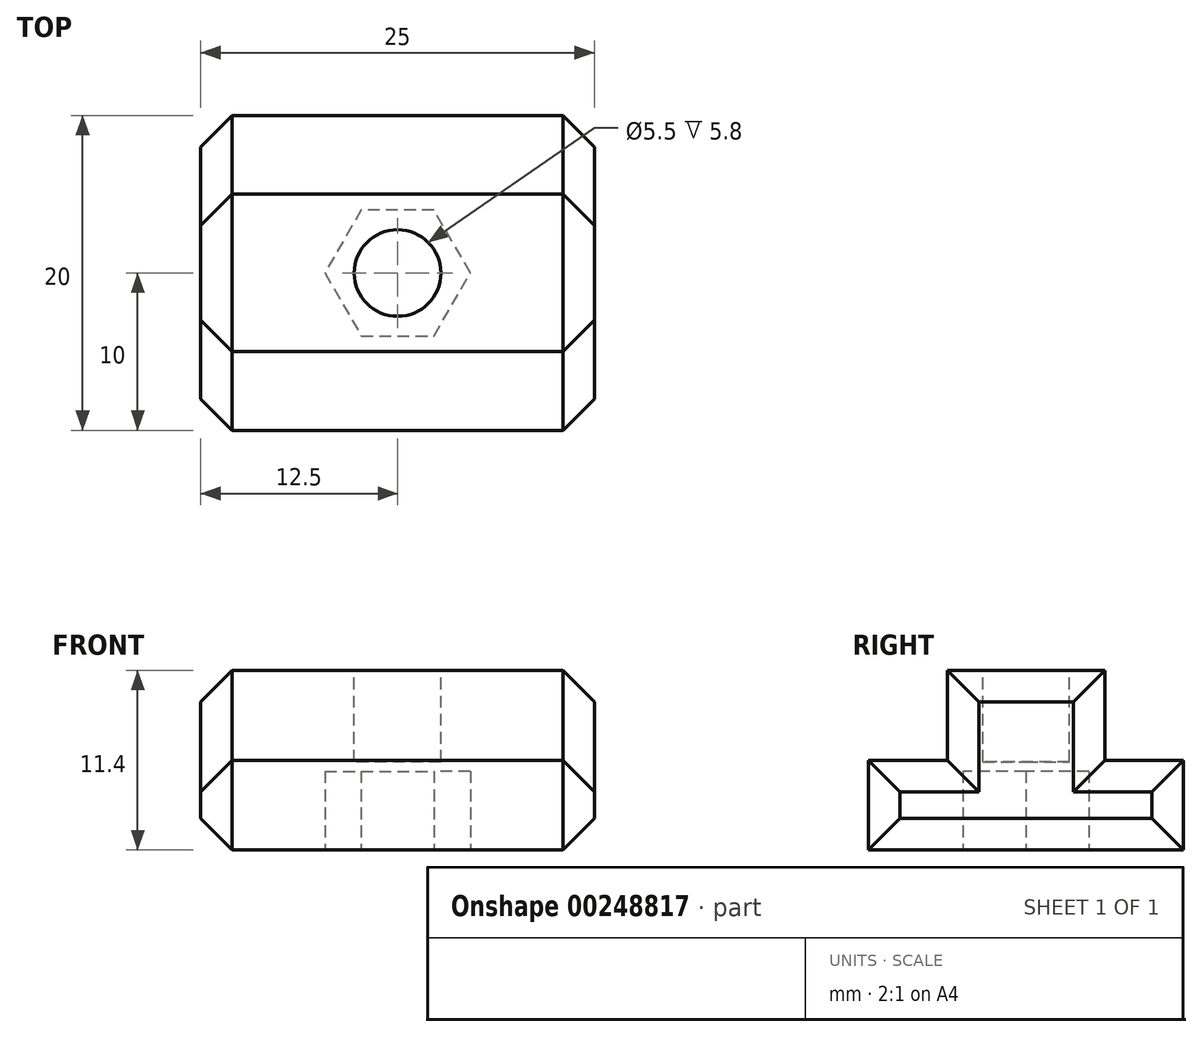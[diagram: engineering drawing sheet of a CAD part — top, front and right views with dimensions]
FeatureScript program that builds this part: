
annotation { "Feature Type Name" : "Feature", "Feature Type Description" : "" }
export const myFeature = defineFeature(function(context is Context, id is Id, definition is map)
    precondition{}
    {
        {
            var Q0;
            Q0=qCreatedBy(makeId("Right.planeOp"),FACE);
            var sketch = newSketch(context, id + "F0", { "sketchPlane" : qUnion([Q0])});
            skLineSegment(sketch, "E0", {"start": v(0, 5.7) * mm, "end": v(5, 5.7) * mm});
            skLineSegment(sketch, "E1", {"start": v(5, 5.7) * mm, "end": v(5, 0) * mm});
            skLineSegment(sketch, "E2", {"start": v(5, 0) * mm, "end": v(10, 0) * mm});
            skLineSegment(sketch, "E3", {"start": v(10, 0) * mm, "end": v(10, -5.7) * mm});
            skLineSegment(sketch, "E4", {"start": v(10, -5.7) * mm, "end": v(0, -5.7) * mm});
            skLineSegment(sketch, "E5.MirrorCS", {"start": v(0, 5.7) * mm, "end": v(-5, 5.7) * mm});
            skLineSegment(sketch, "E6.MirrorCS", {"start": v(-5, 0) * mm, "end": v(-10, 0) * mm});
            skLineSegment(sketch, "E7.MirrorCS", {"start": v(-10, -5.7) * mm, "end": v(0, -5.7) * mm});
            skLineSegment(sketch, "E8.MirrorCS", {"start": v(-5, 5.7) * mm, "end": v(-5, 0) * mm});
            skLineSegment(sketch, "E9.MirrorCS", {"start": v(-10, 0) * mm, "end": v(-10, -5.7) * mm});
            skSolve(sketch);
        }
        {
            var Q0;
            Q0=makeQuery(id+"F0.imprint","IMPRINT",FACE,{"disambiguationData":[TD([[makeQuery(id+"F0.imprint","IMPRINT",EDGE,{"derivedFrom":sQuery(id+"F0.wireOp",EDGE,"E0")}),-1.0]])]});
            extrude(context, id + "F1", {"entities" : qUnion([Q0]), "depth" : 25 * mm, "symmetric" : true});
        }
        {
            var Q0;
            Q0=makeQuery(id+"F1.opExtrude","SWEPT_FACE",FACE,{"disambiguationData":[OSD([sQuery(id+"F0.wireOp",EDGE,"E4"),sQuery(id+"F0.wireOp",EDGE,"E7.MirrorCS")])]});
            var sketch = newSketch(context, id + "F2", { "sketchPlane" : qUnion([Q0])});
            skCircle(sketch, "E10.cCircle", {"center": v(0, 0) * mm, "radius": 4 * mm, "construction": true});
            skLineSegment(sketch, "E10.0", {"start": v(-2.3, 4) * mm, "end": v(2.3, 4) * mm});
            skLineSegment(sketch, "E10.1", {"start": v(2.3, 4) * mm, "end": v(4.62, 0) * mm});
            skLineSegment(sketch, "E10.2", {"start": v(4.62, 0) * mm, "end": v(2.3, -4) * mm});
            skLineSegment(sketch, "E10.3", {"start": v(2.3, -4) * mm, "end": v(-2.3, -4) * mm});
            skLineSegment(sketch, "E10.4", {"start": v(-2.3, -4) * mm, "end": v(-4.62, 0) * mm});
            skLineSegment(sketch, "E10.5", {"start": v(-4.62, 0) * mm, "end": v(-2.3, 4) * mm});
            skPoint(sketch, "E10.0.midPoint", {"position": v(0, 4) * mm});
            skSolve(sketch);
        }
        {
            var Q0;
            Q0=makeQuery(id+"F2.imprint","IMPRINT",FACE,{"disambiguationData":[TD([[makeQuery(id+"F2.imprint","IMPRINT",EDGE,{"derivedFrom":sQuery(id+"F2.wireOp",EDGE,"E10.0")}),-1.0]])]});
            extrude(context, id + "F3", {"entities" : qUnion([Q0]), "operationType" : NewBodyOperationType.REMOVE, "oppositeDirection" : true, "depth" : 5 * mm, "offsetDistance" : 25 * mm});
        }
        {
            var Q0;
            Q0=makeQuery(id+"F1.opExtrude","SWEPT_FACE",FACE,{"disambiguationData":[OSD([sQuery(id+"F0.wireOp",EDGE,"E0"),sQuery(id+"F0.wireOp",EDGE,"E5.MirrorCS")])]});
            var sketch = newSketch(context, id + "F4", { "sketchPlane" : qUnion([Q0])});
            skCircle(sketch, "E11", {"center": v(0, 0) * mm, "radius": 2.75 * mm});
            skSolve(sketch);
        }
        {
            var Q0;
            Q0=makeQuery(id+"F4.imprint","IMPRINT",FACE,{"disambiguationData":[TD([[makeQuery(id+"F4.imprint","IMPRINT",EDGE,{"derivedFrom":sQuery(id+"F4.wireOp",EDGE,"E11")}),1.0]])]});
            extrude(context, id + "F5", {"entities" : qUnion([Q0]), "operationType" : NewBodyOperationType.REMOVE, "oppositeDirection" : true, "depth" : 5.8 * mm});
        }
        {
            var Q0;
            Q0=makeQuery(id+"F1.opExtrude","CAP_EDGE",EDGE,{"disambiguationData":[OSD([sQuery(id+"F0.wireOp",EDGE,"E0"),sQuery(id+"F0.wireOp",EDGE,"E5.MirrorCS")])],"isStart":false});
            var Q1;
            Q1=makeQuery(id+"F1.opExtrude","CAP_EDGE",EDGE,{"disambiguationData":[OSD([sQuery(id+"F0.wireOp",EDGE,"E8.MirrorCS")])],"isStart":false});
            var Q2;
            Q2=makeQuery(id+"F1.opExtrude","CAP_EDGE",EDGE,{"disambiguationData":[OSD([sQuery(id+"F0.wireOp",EDGE,"E6.MirrorCS")])],"isStart":false});
            var Q3;
            Q3=makeQuery(id+"F1.opExtrude","CAP_EDGE",EDGE,{"disambiguationData":[OSD([sQuery(id+"F0.wireOp",EDGE,"E2")])],"isStart":false});
            var Q4;
            Q4=makeQuery(id+"F1.opExtrude","CAP_EDGE",EDGE,{"disambiguationData":[OSD([sQuery(id+"F0.wireOp",EDGE,"E1")])],"isStart":false});
            var Q5;
            Q5=makeQuery(id+"F1.opExtrude","CAP_EDGE",EDGE,{"disambiguationData":[OSD([sQuery(id+"F0.wireOp",EDGE,"E9.MirrorCS")])],"isStart":false});
            var Q6;
            Q6=makeQuery(id+"F1.opExtrude","CAP_EDGE",EDGE,{"disambiguationData":[OSD([sQuery(id+"F0.wireOp",EDGE,"E3")])],"isStart":false});
            var Q7;
            Q7=makeQuery(id+"F1.opExtrude","CAP_EDGE",EDGE,{"disambiguationData":[OSD([sQuery(id+"F0.wireOp",EDGE,"E9.MirrorCS")])],"isStart":true});
            var Q8;
            Q8=makeQuery(id+"F1.opExtrude","CAP_EDGE",EDGE,{"disambiguationData":[OSD([sQuery(id+"F0.wireOp",EDGE,"E6.MirrorCS")])],"isStart":true});
            var Q9;
            Q9=makeQuery(id+"F1.opExtrude","CAP_EDGE",EDGE,{"disambiguationData":[OSD([sQuery(id+"F0.wireOp",EDGE,"E8.MirrorCS")])],"isStart":true});
            var Q10;
            Q10=makeQuery(id+"F1.opExtrude","CAP_EDGE",EDGE,{"disambiguationData":[OSD([sQuery(id+"F0.wireOp",EDGE,"E0"),sQuery(id+"F0.wireOp",EDGE,"E5.MirrorCS")])],"isStart":true});
            var Q11;
            Q11=makeQuery(id+"F1.opExtrude","CAP_EDGE",EDGE,{"disambiguationData":[OSD([sQuery(id+"F0.wireOp",EDGE,"E1")])],"isStart":true});
            var Q12;
            Q12=makeQuery(id+"F1.opExtrude","CAP_EDGE",EDGE,{"disambiguationData":[OSD([sQuery(id+"F0.wireOp",EDGE,"E2")])],"isStart":true});
            var Q13;
            Q13=makeQuery(id+"F1.opExtrude","CAP_EDGE",EDGE,{"disambiguationData":[OSD([sQuery(id+"F0.wireOp",EDGE,"E3")])],"isStart":true});
            var Q14;
            Q14=makeQuery(id+"F1.opExtrude","CAP_EDGE",EDGE,{"disambiguationData":[OSD([sQuery(id+"F0.wireOp",EDGE,"E4"),sQuery(id+"F0.wireOp",EDGE,"E7.MirrorCS")])],"isStart":true});
            var Q15;
            Q15=makeQuery(id+"F1.opExtrude","CAP_EDGE",EDGE,{"disambiguationData":[OSD([sQuery(id+"F0.wireOp",EDGE,"E4"),sQuery(id+"F0.wireOp",EDGE,"E7.MirrorCS")])],"isStart":false});
            chamfer(context, id + "F6", {"entities" : qUnion([Q0, Q1, Q2, Q3, Q4, Q5, Q6, Q7, Q8, Q9, Q10, Q11, Q12, Q13, Q14, Q15]), "width" : 2 * mm, "tangentPropagation" : true});
        }
    });
